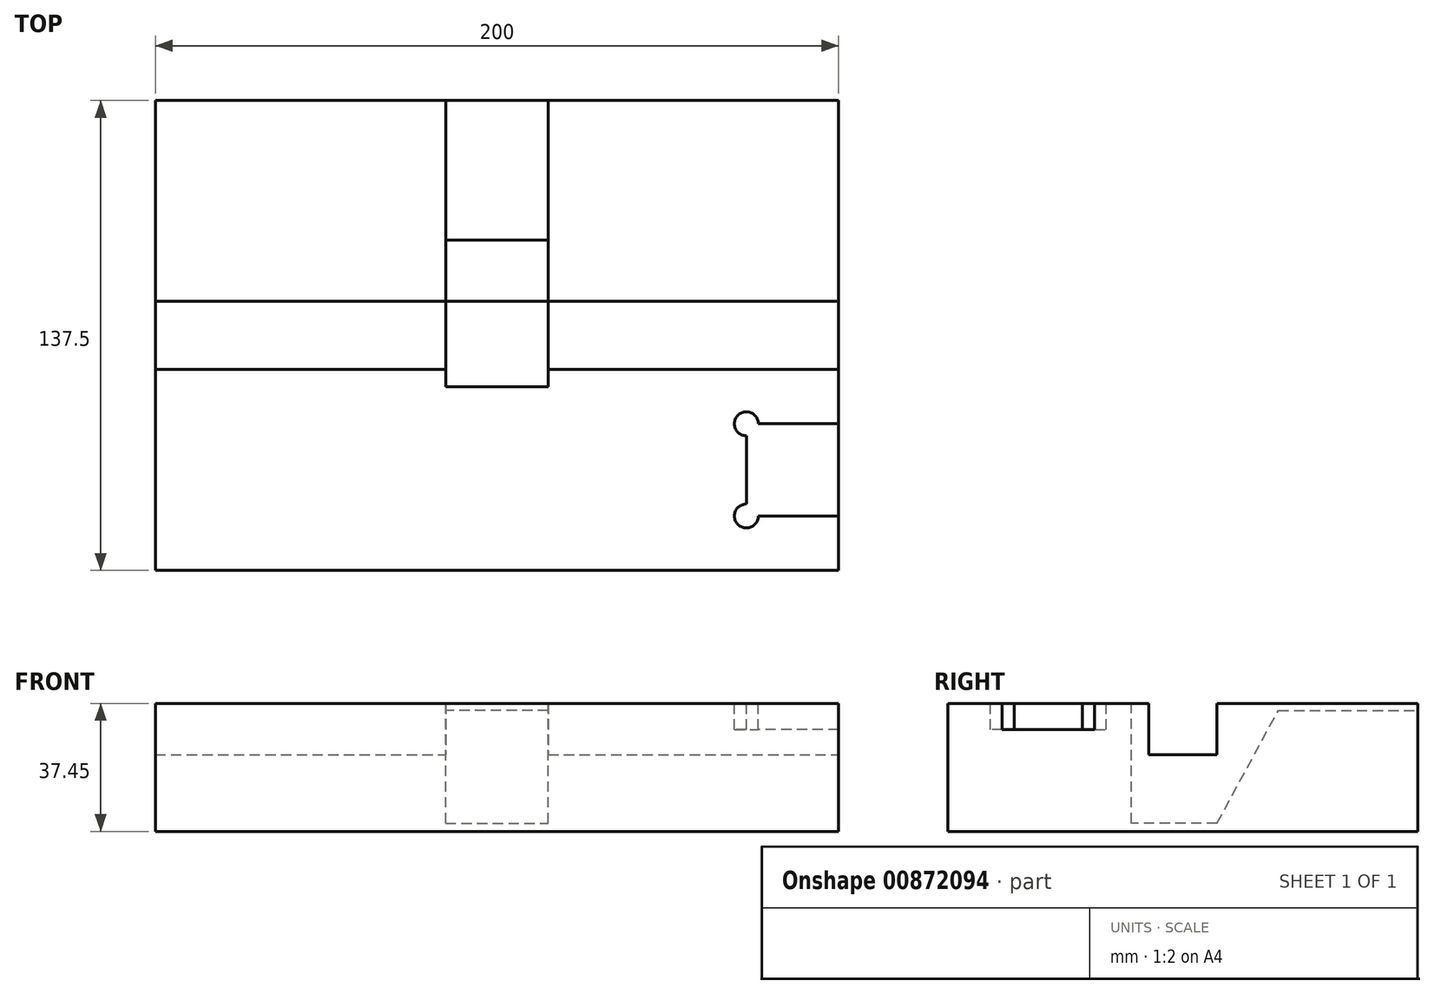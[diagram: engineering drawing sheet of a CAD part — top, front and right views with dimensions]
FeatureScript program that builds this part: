
annotation { "Feature Type Name" : "Feature", "Feature Type Description" : "" }
export const myFeature = defineFeature(function(context is Context, id is Id, definition is map)
    precondition{}
    {
        {
            var Q0;
            Q0=qCreatedBy(makeId("Top.planeOp"),FACE);
            var sketch = newSketch(context, id + "F0", { "sketchPlane" : qUnion([Q0])});
            skLineSegment(sketch, "E0.bottom", {"start": v(-100, 68.75) * mm, "end": v(100, 68.75) * mm});
            skLineSegment(sketch, "E0.top", {"start": v(-100, -68.75) * mm, "end": v(100, -68.75) * mm});
            skLineSegment(sketch, "E0.left", {"start": v(-100, 68.75) * mm, "end": v(-100, -68.75) * mm});
            skLineSegment(sketch, "E0.right", {"start": v(100, 68.75) * mm, "end": v(100, -68.75) * mm});
            skPoint(sketch, "E0.middle", {"position": v(0, 0) * mm});
            skSolve(sketch);
        }
        {
            var Q0;
            Q0 = qSketchRegion(id + "F0", true);
            extrude(context, id + "F1", {"entities" : qUnion([Q0]), "depth" : 37.45 * mm, "offsetDistance" : 25 * mm});
        }
        {
            var Q0;
            Q0=makeQuery(id+"F1.opExtrude","CAP_FACE",FACE,{"disambiguationData":[OSD([sQuery(id+"F0.wireOp",EDGE,"E0.bottom"),sQuery(id+"F0.wireOp",EDGE,"E0.top"),sQuery(id+"F0.wireOp",EDGE,"E0.left"),sQuery(id+"F0.wireOp",EDGE,"E0.right")])],"isStart":false});
            var sketch = newSketch(context, id + "F2", { "sketchPlane" : qUnion([Q0])});
            skLineSegment(sketch, "E1.bottom", {"start": v(-100, 10) * mm, "end": v(100, 10) * mm});
            skLineSegment(sketch, "E1.top", {"start": v(-100, -10) * mm, "end": v(100, -10) * mm});
            skLineSegment(sketch, "E1.left", {"start": v(-100, 10) * mm, "end": v(-100, -10) * mm});
            skLineSegment(sketch, "E1.right", {"start": v(100, 10) * mm, "end": v(100, -10) * mm});
            skPoint(sketch, "E1.middle", {"position": v(0, 0) * mm});
            skSolve(sketch);
        }
        {
            var Q0;
            Q0 = qSketchRegion(id + "F2", true);
            extrude(context, id + "F3", {"entities" : qUnion([Q0]), "operationType" : NewBodyOperationType.REMOVE, "oppositeDirection" : true, "depth" : 15 * mm, "offsetDistance" : 25 * mm});
        }
        {
            var Q0;
            {var subQ0=sQuery(id+"F0.wireOp",EDGE,"E0.bottom");var subQ1=sQuery(id+"F0.wireOp",EDGE,"E0.right");var subQ2=sQuery(id+"F0.wireOp",EDGE,"E0.left");Q0=makeQuery(id+"F3.boolean.opBoolean","SPLIT",FACE,{"disambiguationData":[TD([makeQuery(id+"F1.opExtrude","SWEPT_FACE",FACE,{"disambiguationData":[OSD([subQ0])]})])],"derivedFrom":makeQuery(id+"F1.opExtrude","CAP_FACE",FACE,{"disambiguationData":[OSD([subQ0,sQuery(id+"F0.wireOp",EDGE,"E0.top"),subQ2,subQ1])],"isStart":false})});}
            var sketch = newSketch(context, id + "F4", { "sketchPlane" : qUnion([Q0])});
            skLineSegment(sketch, "E2.top", {"start": v(-11.5, 10) * mm, "end": v(11.5, 10) * mm});
            skLineSegment(sketch, "E3", {"start": v(0, 68.75) * mm, "end": v(0, 10) * mm, "construction": true});
            skLineSegment(sketch, "E4.bottom", {"start": v(-15, 10) * mm, "end": v(15, 10) * mm});
            skLineSegment(sketch, "E4.top", {"start": v(-15, -10) * mm, "end": v(15, -10) * mm});
            skLineSegment(sketch, "E4.left", {"start": v(-15, 10) * mm, "end": v(-15, -10) * mm});
            skLineSegment(sketch, "E4.right", {"start": v(15, 10) * mm, "end": v(15, -10) * mm});
            skPoint(sketch, "E4.middle", {"position": v(0, 0) * mm});
            skLineSegment(sketch, "E5.bottom", {"start": v(-15, 10) * mm, "end": v(28.37, 10) * mm});
            skLineSegment(sketch, "E6.top", {"start": v(-15, -15) * mm, "end": v(15, -15) * mm});
            skLineSegment(sketch, "E6.left", {"start": v(-15, -10) * mm, "end": v(-15, -15) * mm});
            skLineSegment(sketch, "E6.right", {"start": v(15, -10) * mm, "end": v(15, -15) * mm});
            skSolve(sketch);
        }
        {
            var Q0;
            Q0 = qSketchRegion(id + "F4", true);
            extrude(context, id + "F5", {"entities" : qUnion([Q0]), "operationType" : NewBodyOperationType.REMOVE, "oppositeDirection" : true, "depth" : 35 * mm, "offsetDistance" : 25 * mm});
        }
        {
            var Q0;
            Q0=qCreatedBy(makeId("Right.planeOp"),FACE);
            var sketch = newSketch(context, id + "F6", { "sketchPlane" : qUnion([Q0])});
            skLineSegment(sketch, "E7", {"start": v(10, 2.45) * mm, "end": v(29.03, 37.45) * mm});
            skLineSegment(sketch, "E8", {"start": v(29.03, 37.45) * mm, "end": v(10, 37.45) * mm});
            skLineSegment(sketch, "E9", {"start": v(10, 37.45) * mm, "end": v(10, 2.45) * mm});
            skLineSegment(sketch, "E10", {"start": v(27.94, 35.45) * mm, "end": v(68.75, 35.45) * mm});
            skLineSegment(sketch, "E11", {"start": v(68.75, 35.45) * mm, "end": v(68.75, 37.45) * mm});
            skLineSegment(sketch, "E12", {"start": v(68.75, 37.45) * mm, "end": v(29.03, 37.45) * mm});
            skSolve(sketch);
        }
        {
            var Q0;
            Q0 = qSketchRegion(id + "F6", true);
            extrude(context, id + "F7", {"entities" : qUnion([Q0]), "operationType" : NewBodyOperationType.REMOVE, "endBound" : BoundingType.SYMMETRIC, "depth" : 30 * mm, "offsetDistance" : 25 * mm});
        }
        {
            var Q0;
            {var subQ0=sQuery(id+"F0.wireOp",EDGE,"E0.top");var subQ1=sQuery(id+"F0.wireOp",EDGE,"E0.left");var subQ2=sQuery(id+"F0.wireOp",EDGE,"E0.right");Q0=makeQuery(id+"F3.boolean.opBoolean","SPLIT",FACE,{"disambiguationData":[TD([makeQuery(id+"F1.opExtrude","SWEPT_FACE",FACE,{"disambiguationData":[OSD([subQ0])]})])],"derivedFrom":makeQuery(id+"F1.opExtrude","CAP_FACE",FACE,{"disambiguationData":[OSD([sQuery(id+"F0.wireOp",EDGE,"E0.bottom"),subQ0,subQ1,subQ2])],"isStart":false})});}
            var sketch = newSketch(context, id + "F8", { "sketchPlane" : qUnion([Q0])});
            skLineSegment(sketch, "E13.bottom", {"start": v(100, -52.88) * mm, "end": v(73, -52.88) * mm});
            skLineSegment(sketch, "E13.top", {"start": v(100, -25.88) * mm, "end": v(73, -25.88) * mm});
            skLineSegment(sketch, "E13.left", {"start": v(100, -52.88) * mm, "end": v(100, -25.88) * mm});
            skLineSegment(sketch, "E13.right", {"start": v(73, -52.88) * mm, "end": v(73, -25.88) * mm});
            skLineSegment(sketch, "E14", {"start": v(100, -39.38) * mm, "end": v(-100, -39.38) * mm, "construction": true});
            skLineSegment(sketch, "E15", {"start": v(100, -39.38) * mm, "end": v(73, -39.38) * mm, "construction": true});
            skCircle(sketch, "E16", {"center": v(73, -25.88) * mm, "radius": 3.5 * mm});
            skCircle(sketch, "E17", {"center": v(73, -52.88) * mm, "radius": 3.5 * mm});
            skSolve(sketch);
        }
        {
            var Q0;
            Q0 = qSketchRegion(id + "F8", true);
            extrude(context, id + "F9", {"entities" : qUnion([Q0]), "operationType" : NewBodyOperationType.REMOVE, "oppositeDirection" : true, "depth" : 7.6 * mm, "offsetDistance" : 25 * mm});
        }
    });
